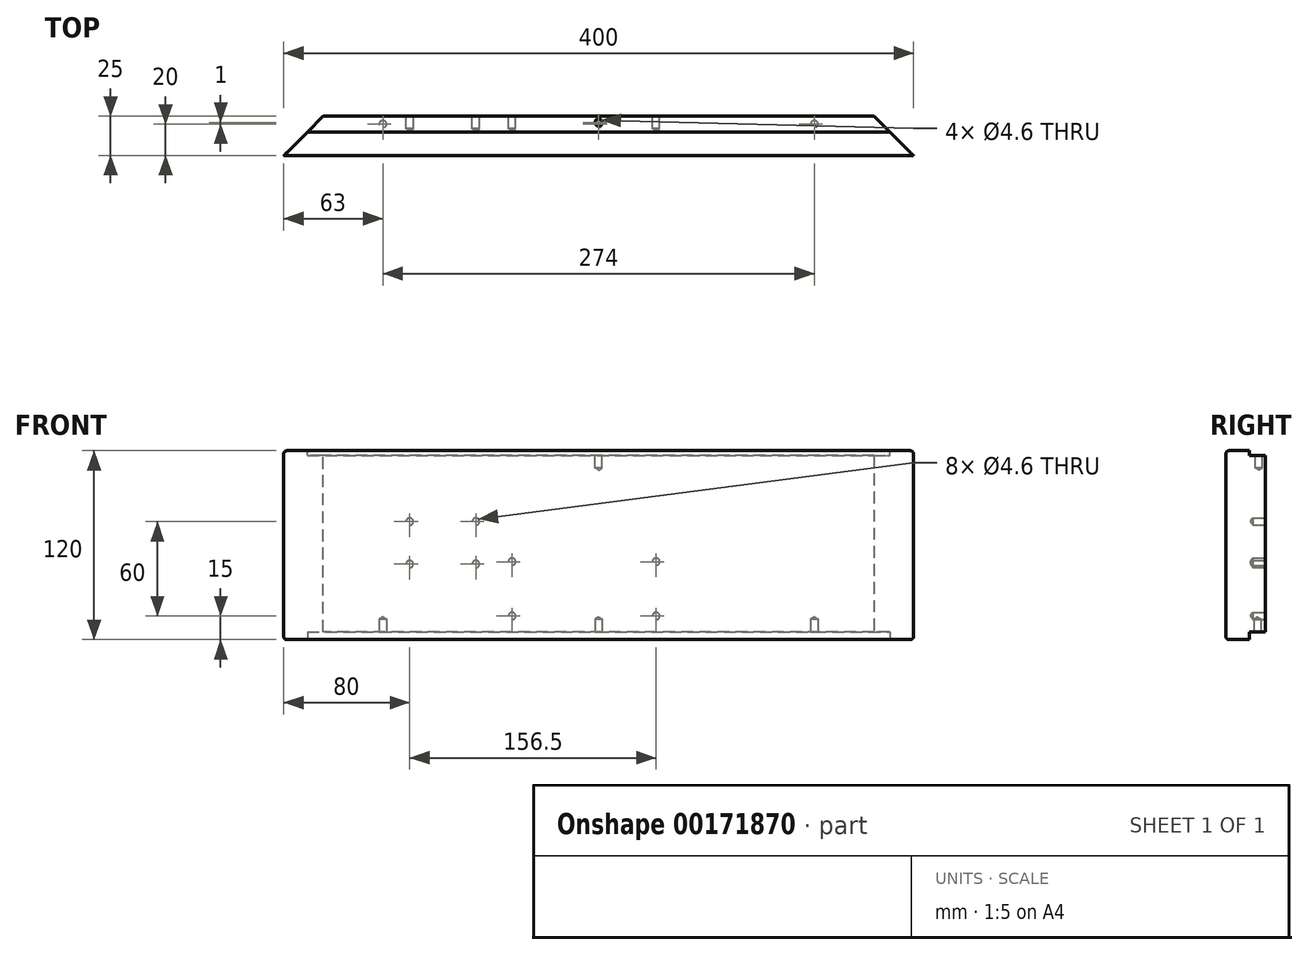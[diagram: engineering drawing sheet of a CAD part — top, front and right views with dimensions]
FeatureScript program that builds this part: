
annotation { "Feature Type Name" : "Feature", "Feature Type Description" : "" }
export const myFeature = defineFeature(function(context is Context, id is Id, definition is map)
    precondition{}
    {
        {
            var Q0;
            Q0=qCreatedBy(makeId("Front.planeOp"),FACE);
            var sketch = newSketch(context, id + "F0", { "sketchPlane" : qUnion([Q0])});
            skLineSegment(sketch, "E0.bottom", {"start": v(200, -60) * mm, "end": v(-200, -60) * mm});
            skLineSegment(sketch, "E0.top", {"start": v(200, 60) * mm, "end": v(-200, 60) * mm});
            skLineSegment(sketch, "E0.left", {"start": v(200, -60) * mm, "end": v(200, 60) * mm});
            skLineSegment(sketch, "E0.right", {"start": v(-200, -60) * mm, "end": v(-200, 60) * mm});
            skPoint(sketch, "E0.middle", {"position": v(0, 0) * mm});
            skSolve(sketch);
        }
        {
            var Q0;
            Q0=makeQuery(id+"F0.imprint","IMPRINT",FACE,{"disambiguationData":[TD([[makeQuery(id+"F0.imprint","IMPRINT",EDGE,{"derivedFrom":sQuery(id+"F0.wireOp",EDGE,"E0.bottom")}),-1.0]])]});
            extrude(context, id + "F1", {"entities" : qUnion([Q0]), "depth" : 25 * mm});
        }
        {
            var Q0;
            Q0=makeQuery(id+"F1.opExtrude","CAP_EDGE",EDGE,{"disambiguationData":[OSD([sQuery(id+"F0.wireOp",EDGE,"E0.right")])],"isStart":true});
            var Q1;
            Q1=makeQuery(id+"F1.opExtrude","CAP_EDGE",EDGE,{"disambiguationData":[OSD([sQuery(id+"F0.wireOp",EDGE,"E0.left")])],"isStart":true});
            chamfer(context, id + "F2", {"entities" : qUnion([Q0, Q1]), "width" : 25 * mm, "tangentPropagation" : true});
        }
        {
            var Q0;
            Q0=makeQuery(id+"F1.opExtrude","SWEPT_FACE",FACE,{"disambiguationData":[OSD([sQuery(id+"F0.wireOp",EDGE,"E0.top")])]});
            var sketch = newSketch(context, id + "F3", { "sketchPlane" : qUnion([Q0])});
            skLineSegment(sketch, "E1", {"start": v(-185, -10) * mm, "end": v(185, -10) * mm});
            skSolve(sketch);
        }
        {
            var Q0;
            {var subQ0=sQuery(id+"F3.wireOp",EDGE,"E1");Q0=makeQuery(id+"F3.imprint","IMPRINT",FACE,{"disambiguationData":[TD([[makeQuery(id+"F3.imprint","IMPRINT",EDGE,{"derivedFrom":subQ0}),1.0]])]});}
            extrude(context, id + "F4", {"entities" : qUnion([Q0]), "operationType" : NewBodyOperationType.REMOVE, "oppositeDirection" : true, "depth" : 3 * mm});
        }
        {
            var Q0;
            Q0=makeQuery(id+"F1.opExtrude","SWEPT_FACE",FACE,{"disambiguationData":[OSD([sQuery(id+"F0.wireOp",EDGE,"E0.bottom")])]});
            var sketch = newSketch(context, id + "F5", { "sketchPlane" : qUnion([Q0])});
            skLineSegment(sketch, "E2", {"start": v(-185, 10) * mm, "end": v(185, 10) * mm});
            skSolve(sketch);
        }
        {
            var Q0;
            {var subQ0=sQuery(id+"F5.wireOp",EDGE,"E2");Q0=makeQuery(id+"F5.imprint","IMPRINT",FACE,{"disambiguationData":[TD([[makeQuery(id+"F5.imprint","IMPRINT",EDGE,{"derivedFrom":subQ0}),-1.0]])]});}
            extrude(context, id + "F6", {"entities" : qUnion([Q0]), "operationType" : NewBodyOperationType.REMOVE, "oppositeDirection" : true, "depth" : 5 * mm});
        }
        {
            var Q0;
            Q0=makeQuery(id+"F0.imprint","IMPRINT",FACE,{"disambiguationData":[TD([[makeQuery(id+"F0.imprint","IMPRINT",EDGE,{"derivedFrom":sQuery(id+"F0.wireOp",EDGE,"E0.bottom")}),-1.0]])]});
            var sketch = newSketch(context, id + "F7", { "sketchPlane" : qUnion([Q0])});
            skLineSegment(sketch, "E3", {"start": v(-14.15, 15) * mm, "end": v(-150.88, 15) * mm, "construction": true});
            skLineSegment(sketch, "E4", {"start": v(-14.55, -12) * mm, "end": v(-153.09, -12) * mm, "construction": true});
            skLineSegment(sketch, "E5", {"start": v(-120, 39.85) * mm, "end": v(-120, -25.61) * mm, "construction": true});
            skLineSegment(sketch, "E6", {"start": v(-78, 39.45) * mm, "end": v(-78, -25.01) * mm, "construction": true});
            skPoint(sketch, "E7", {"position": v(-78, 15) * mm});
            skPoint(sketch, "E8", {"position": v(-120, 15) * mm});
            skPoint(sketch, "E9", {"position": v(-120, -12) * mm});
            skPoint(sketch, "E10", {"position": v(-78, -12) * mm});
            skLineSegment(sketch, "E11", {"start": v(-55, 67.03) * mm, "end": v(-55, -62.88) * mm, "construction": true});
            skLineSegment(sketch, "E12", {"start": v(36.5, 70.94) * mm, "end": v(36.5, -69.72) * mm, "construction": true});
            skLineSegment(sketch, "E13", {"start": v(88.88, -10.5) * mm, "end": v(-62.51, -10.5) * mm, "construction": true});
            skLineSegment(sketch, "E14", {"start": v(79.6, -45) * mm, "end": v(-63.73, -45) * mm, "construction": true});
            skPoint(sketch, "E15", {"position": v(-55, -10.5) * mm});
            skPoint(sketch, "E16", {"position": v(36.5, -10.5) * mm});
            skPoint(sketch, "E17", {"position": v(36.5, -45) * mm});
            skPoint(sketch, "E18", {"position": v(-55, -45) * mm});
            skSolve(sketch);
        }
        {
            var Q0;
            Q0=sQuery(id+"F7.wireOp",VERTEX,"e11a47ab-27d6-4492-a48e-845e7b2e10df");
            var Q1;
            Q1=sQuery(id+"F7.wireOp",VERTEX,"362fe969-215c-4ec1-94ff-277edc13dcfb");
            var Q2;
            Q2=sQuery(id+"F7.wireOp",VERTEX,"E8");
            var Q3;
            Q3=sQuery(id+"F7.wireOp",VERTEX,"E7");
            var Q4;
            Q4=sQuery(id+"F7.wireOp",VERTEX,"E10");
            var Q5;
            Q5=sQuery(id+"F7.wireOp",VERTEX,"E9");
            var Q6;
            Q6=sQuery(id+"F7.wireOp",VERTEX,"e56d426c-e884-4e2d-9bb7-c59f3eda06d3");
            var Q7;
            Q7=sQuery(id+"F7.wireOp",VERTEX,"102f9b56-d853-4af5-9190-722c06e6039e");
            var Q8;
            Q8=sQuery(id+"F7.wireOp",VERTEX,"E18");
            var Q9;
            Q9=sQuery(id+"F7.wireOp",VERTEX,"E17");
            var Q10;
            Q10=sQuery(id+"F7.wireOp",VERTEX,"E16");
            var Q11;
            Q11=sQuery(id+"F7.wireOp",VERTEX,"E15");
            var Q12;
            Q12=makeQuery(id+"F1.opExtrude","SWEPT_BODY",BODY,{"disambiguationData":[OSD([sQuery(id+"F0.wireOp",EDGE,"E0.bottom"),sQuery(id+"F0.wireOp",EDGE,"E0.top"),sQuery(id+"F0.wireOp",EDGE,"E0.left"),sQuery(id+"F0.wireOp",EDGE,"E0.right")])]});
            hole(context, id + "F8", {"style" : HoleStyle.SIMPLE, "endStyle" : HoleEndStyle.BLIND, "oppositeDirection" : true, "holeDiameter" : 4.6 * mm, "holeDepth" : 8 * mm, "startFromSketch" : true, "locations" : qUnion([Q0, Q1, Q2, Q3, Q4, Q5, Q6, Q7, Q8, Q9, Q10, Q11]), "scope" : qUnion([Q12])});
        }
        {
            var Q0;
            Q0=makeQuery(id+"F4.boolean.opBoolean","COPY",FACE,{"derivedFrom":makeQuery(id+"F4.opExtrude","CAP_FACE",FACE,{"disambiguationData":[OSD([sQuery(id+"F0.wireOp",EDGE,"E0.top"),sQuery(id+"F0.wireOp",EDGE,"E0.left"),sQuery(id+"F0.wireOp",EDGE,"E0.right"),sQuery(id+"F3.wireOp",EDGE,"E1")])],"isStart":false})});
            var sketch = newSketch(context, id + "F9", { "sketchPlane" : qUnion([Q0])});
            skLineSegment(sketch, "E19", {"start": v(-168.3, -4) * mm, "end": v(166.3, -4) * mm, "construction": true});
            skLineSegment(sketch, "E20", {"start": v(0, 10.85) * mm, "end": v(0, -15.9) * mm, "construction": true});
            skPoint(sketch, "E20.endSnap0", {"position": v(0, -10) * mm});
            skPoint(sketch, "E21", {"position": v(0, -4) * mm});
            skSolve(sketch);
        }
        {
            var Q0;
            Q0=sQuery(id+"F9.wireOp",VERTEX,"E21");
            var Q1;
            Q1=makeQuery(id+"F1.opExtrude","SWEPT_BODY",BODY,{"disambiguationData":[OSD([sQuery(id+"F0.wireOp",EDGE,"E0.bottom"),sQuery(id+"F0.wireOp",EDGE,"E0.top"),sQuery(id+"F0.wireOp",EDGE,"E0.left"),sQuery(id+"F0.wireOp",EDGE,"E0.right")])]});
            hole(context, id + "F10", {"style" : HoleStyle.SIMPLE, "endStyle" : HoleEndStyle.BLIND, "holeDiameter" : 4.6 * mm, "holeDepth" : 8 * mm, "startFromSketch" : true, "locations" : qUnion([Q0]), "scope" : qUnion([Q1])});
        }
        {
            var Q0;
            Q0=makeQuery(id+"F6.boolean.opBoolean","COPY",FACE,{"derivedFrom":makeQuery(id+"F6.opExtrude","CAP_FACE",FACE,{"disambiguationData":[OSD([sQuery(id+"F0.wireOp",EDGE,"E0.bottom"),sQuery(id+"F0.wireOp",EDGE,"E0.left"),sQuery(id+"F0.wireOp",EDGE,"E0.right"),sQuery(id+"F5.wireOp",EDGE,"E2")])],"isStart":false})});
            var sketch = newSketch(context, id + "F11", { "sketchPlane" : qUnion([Q0])});
            skLineSegment(sketch, "E22", {"start": v(-222.57, 5) * mm, "end": v(216.71, 5) * mm, "construction": true});
            skLineSegment(sketch, "E23", {"start": v(-137, 28.3) * mm, "end": v(-137, -15.54) * mm, "construction": true});
            skLineSegment(sketch, "E24", {"start": v(137, 29.01) * mm, "end": v(137, -22.56) * mm, "construction": true});
            skLineSegment(sketch, "E25", {"start": v(0, 22.52) * mm, "end": v(0, -13.9) * mm, "construction": true});
            skPoint(sketch, "E26", {"position": v(-137, 5) * mm});
            skPoint(sketch, "E27", {"position": v(137, 5) * mm});
            skPoint(sketch, "E28", {"position": v(0, 5) * mm});
            skSolve(sketch);
        }
        {
            var Q0;
            Q0=sQuery(id+"F11.wireOp",VERTEX,"E26");
            var Q1;
            Q1=sQuery(id+"F11.wireOp",VERTEX,"E28");
            var Q2;
            Q2=sQuery(id+"F11.wireOp",VERTEX,"E27");
            var Q3;
            Q3=makeQuery(id+"F1.opExtrude","SWEPT_BODY",BODY,{"disambiguationData":[OSD([sQuery(id+"F0.wireOp",EDGE,"E0.bottom"),sQuery(id+"F0.wireOp",EDGE,"E0.top"),sQuery(id+"F0.wireOp",EDGE,"E0.left"),sQuery(id+"F0.wireOp",EDGE,"E0.right")])]});
            hole(context, id + "F12", {"style" : HoleStyle.SIMPLE, "endStyle" : HoleEndStyle.BLIND, "holeDiameter" : 4.6 * mm, "holeDepth" : 8 * mm, "startFromSketch" : true, "locations" : qUnion([Q0, Q1, Q2]), "scope" : qUnion([Q3])});
        }
        {
            var Q0;
            Q0=makeQuery(id+"F1.opExtrude","CAP_EDGE",EDGE,{"disambiguationData":[OSD([sQuery(id+"F0.wireOp",EDGE,"E0.top")])],"isStart":false});
            var Q1;
            Q1=makeQuery(id+"F1.opExtrude","CAP_EDGE",EDGE,{"disambiguationData":[OSD([sQuery(id+"F0.wireOp",EDGE,"E0.bottom")])],"isStart":false});
            fillet(context, id + "F13", {"entities" : qUnion([Q0, Q1]), "radius" : 2 * mm, "tangentPropagation" : true, "allowEdgeOverflow" : false});
        }
    });
